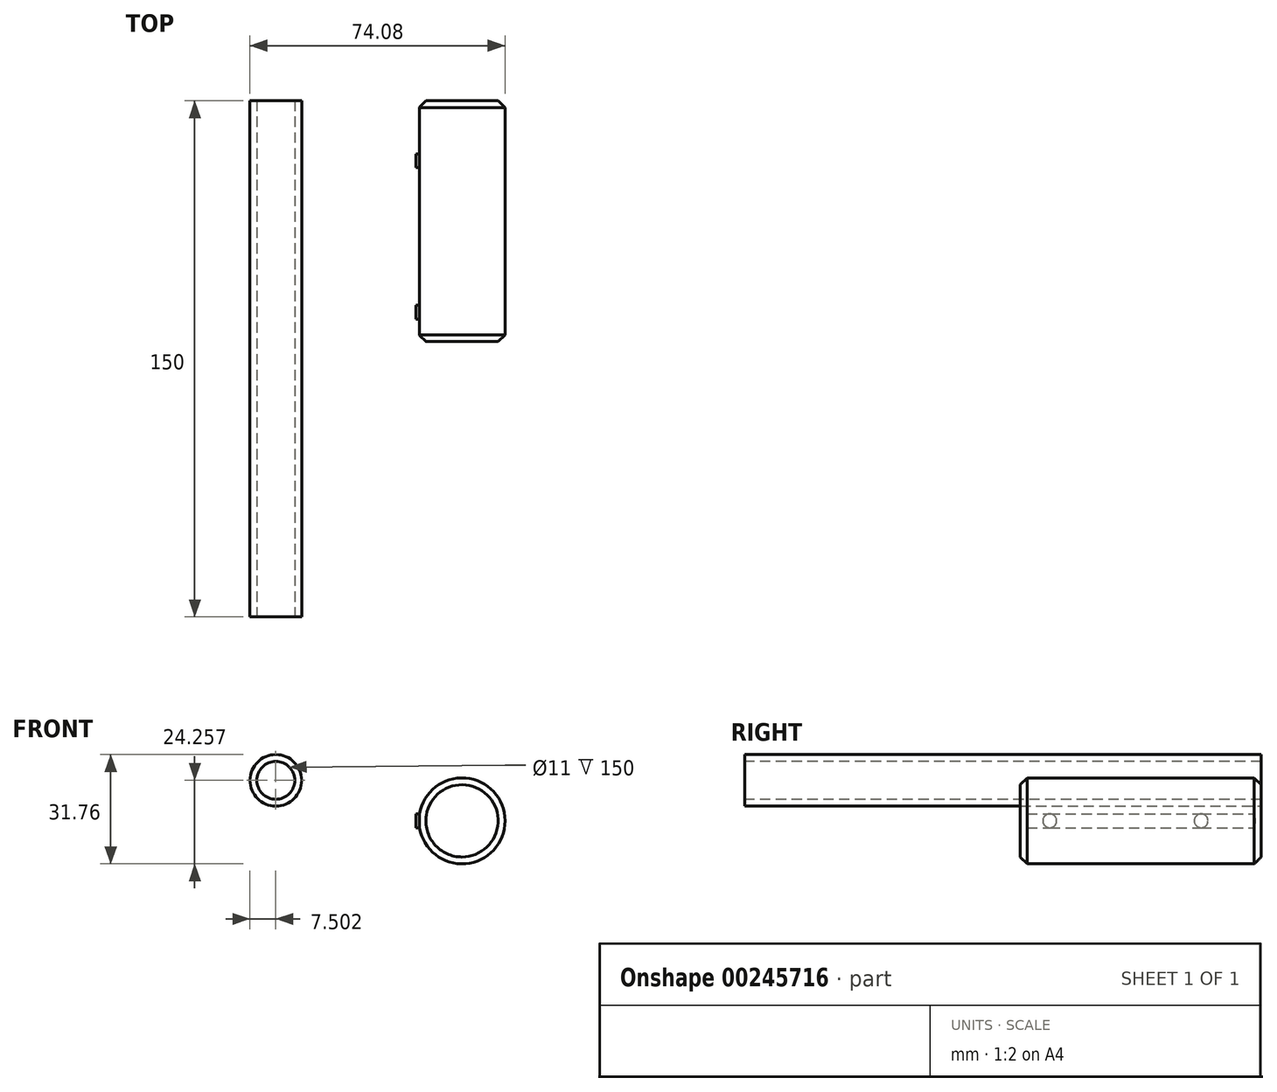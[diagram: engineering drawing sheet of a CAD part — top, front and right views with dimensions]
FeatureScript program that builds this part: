
annotation { "Feature Type Name" : "Feature", "Feature Type Description" : "" }
export const myFeature = defineFeature(function(context is Context, id is Id, definition is map)
    precondition{}
    {
        {
            var Q0;
            Q0=qCreatedBy(makeId("Right.planeOp"),FACE);
            var sketch = newSketch(context, id + "F0", { "sketchPlane" : qUnion([Q0])});
            skLineSegment(sketch, "E0", {"start": v(0, 0) * mm, "end": v(-70, 0) * mm});
            skSolve(sketch);
        }
        {
            var Q0;
            Q0=qCreatedBy(makeId("Front.planeOp"),FACE);
            var sketch = newSketch(context, id + "F1", { "sketchPlane" : qUnion([Q0])});
            skCircle(sketch, "E1", {"center": v(0, 0) * mm, "radius": 12.5 * mm});
            skSolve(sketch);
        }
        {
            var Q0;
            Q0=makeQuery(id+"F1.imprint","IMPRINT",FACE,{"disambiguationData":[TD([[makeQuery(id+"F1.imprint","IMPRINT",EDGE,{"derivedFrom":sQuery(id+"F1.wireOp",EDGE,"E1")}),1.0]])]});
            var Q1;
            Q1=sQuery(id+"F0.wireOp",EDGE,"E0");
            sweep(context, id + "F2", {"profiles" : qUnion([Q0]), "path" : qUnion([Q1])});
        }
        {
            var Q0;
            Q0=makeQuery(id+"F2.opSweep","CAP_FACE",FACE,{"disambiguationData":[OSD([sQuery(id+"F0.wireOp",VERTEX,"E0.start"),sQuery(id+"F1.wireOp",EDGE,"E1")])],"isStart":true});
            var sketch = newSketch(context, id + "F3", { "sketchPlane" : qUnion([Q0])});
            skLineSegment(sketch, "E2", {"start": v(0, 0) * mm, "end": v(12.5, 0) * mm, "construction": true});
            skLineSegment(sketch, "E3", {"start": v(12.34, 2) * mm, "end": v(12.34, -2) * mm});
            skSolve(sketch);
        }
        {
            var Q0;
            {var subQ0=sQuery(id+"F3.wireOp",EDGE,"E3");Q0=makeQuery(id+"F3.imprint","IMPRINT",FACE,{"disambiguationData":[TD([[makeQuery(id+"F3.imprint","IMPRINT",EDGE,{"derivedFrom":subQ0}),1.0]])]});}
            extrude(context, id + "F4", {"entities" : qUnion([Q0]), "operationType" : NewBodyOperationType.REMOVE, "oppositeDirection" : true, "depth" : 555 * mm});
        }
        {
            var Q0;
            Q0=makeQuery(id+"F4.boolean.opBoolean","COPY",FACE,{"derivedFrom":makeQuery(id+"F4.opExtrude","SWEPT_FACE",FACE,{"disambiguationData":[OSD([sQuery(id+"F3.wireOp",EDGE,"E3")])]})});
            var sketch = newSketch(context, id + "F5", { "sketchPlane" : qUnion([Q0])});
            skLineSegment(sketch, "E4", {"start": v(0, 0) * mm, "end": v(70, 0) * mm, "construction": true});
            skCircle(sketch, "E5", {"center": v(17.46, 0) * mm, "radius": 2 * mm});
            skCircle(sketch, "E6", {"center": v(61.43, 0) * mm, "radius": 2 * mm});
            skSolve(sketch);
        }
        {
            var Q0;
            Q0 = qSketchRegion(id + "F5", true);
            extrude(context, id + "F6", {"entities" : qUnion([Q0]), "operationType" : NewBodyOperationType.ADD, "depth" : 5 * mm});
        }
        {
            var Q0;
            Q0=qCreatedBy(makeId("Front.planeOp"),FACE);
            var sketch = newSketch(context, id + "F7", { "sketchPlane" : qUnion([Q0])});
            skCircle(sketch, "E7", {"center": v(-54.08, 11.76) * mm, "radius": 7.5 * mm});
            skSolve(sketch);
        }
        {
            var Q0;
            Q0 = qSketchRegion(id + "F7", true);
            extrude(context, id + "F8", {"entities" : qUnion([Q0]), "depth" : 150 * mm});
        }
        {
            var Q0;
            Q0=makeQuery(id+"F8.opExtrude","CAP_FACE",FACE,{"disambiguationData":[OSD([sQuery(id+"F7.wireOp",EDGE,"E7")])],"isStart":false});
            var sketch = newSketch(context, id + "F9", { "sketchPlane" : qUnion([Q0])});
            skCircle(sketch, "E8", {"center": v(-54.08, 11.76) * mm, "radius": 5.5 * mm});
            skSolve(sketch);
        }
        {
            var Q0;
            Q0 = qSketchRegion(id + "F9", true);
            extrude(context, id + "F10", {"entities" : qUnion([Q0]), "operationType" : NewBodyOperationType.REMOVE, "oppositeDirection" : true, "depth" : 999 * mm});
        }
        {
            var Q0;
            Q0=makeQuery(id+"F8.opExtrude","CAP_FACE",FACE,{"disambiguationData":[OSD([sQuery(id+"F7.wireOp",EDGE,"E7")])],"isStart":false});
            var sketch = newSketch(context, id + "F11", { "sketchPlane" : qUnion([Q0])});
            skCircle(sketch, "E9", {"center": v(-54.08, 11.76) * mm, "radius": 5 * mm});
            skPoint(sketch, "E10", {"position": v(-79.32, 11.76) * mm});
            skSolve(sketch);
        }
        {
            var Q0;
            Q0=qCreatedBy(makeId("Top.planeOp"),FACE);
            var sketch = newSketch(context, id + "F12", { "sketchPlane" : qUnion([Q0])});
            skArc(sketch, "E11", {"start": v(-79.4, -150.17) * mm, "mid": v(-66.68, -155.15) * mm, "end": v(-54.02, -150.04) * mm});
            skSolve(sketch);
        }
        {
            var Q0;
            Q0=makeQuery(id+"F2.opSweep","CAP_EDGE",EDGE,{"disambiguationData":[OSD([sQuery(id+"F0.wireOp",VERTEX,"E0.start"),sQuery(id+"F1.wireOp",EDGE,"E1")])],"isStart":true});
            var Q1;
            Q1=makeQuery(id+"F2.opSweep","CAP_EDGE",EDGE,{"disambiguationData":[OSD([sQuery(id+"F0.wireOp",VERTEX,"E0.end"),sQuery(id+"F1.wireOp",EDGE,"E1")])],"isStart":false});
            chamfer(context, id + "F13", {"entities" : qUnion([Q0, Q1]), "width" : 2 * mm, "tangentPropagation" : true});
        }
        {
            var Q0;
            Q0=makeQuery(id+"F6.opExtrude","CAP_FACE",FACE,{"disambiguationData":[OSD([sQuery(id+"F5.wireOp",EDGE,"E6")])],"isStart":false});
            var Q1;
            Q1=makeQuery(id+"F6.opExtrude","CAP_FACE",FACE,{"disambiguationData":[OSD([sQuery(id+"F5.wireOp",EDGE,"E5")])],"isStart":false});
            extrude(context, id + "F14", {"entities" : qUnion([Q0, Q1]), "operationType" : NewBodyOperationType.REMOVE, "oppositeDirection" : true, "depth" : 4 * mm});
        }
    });
